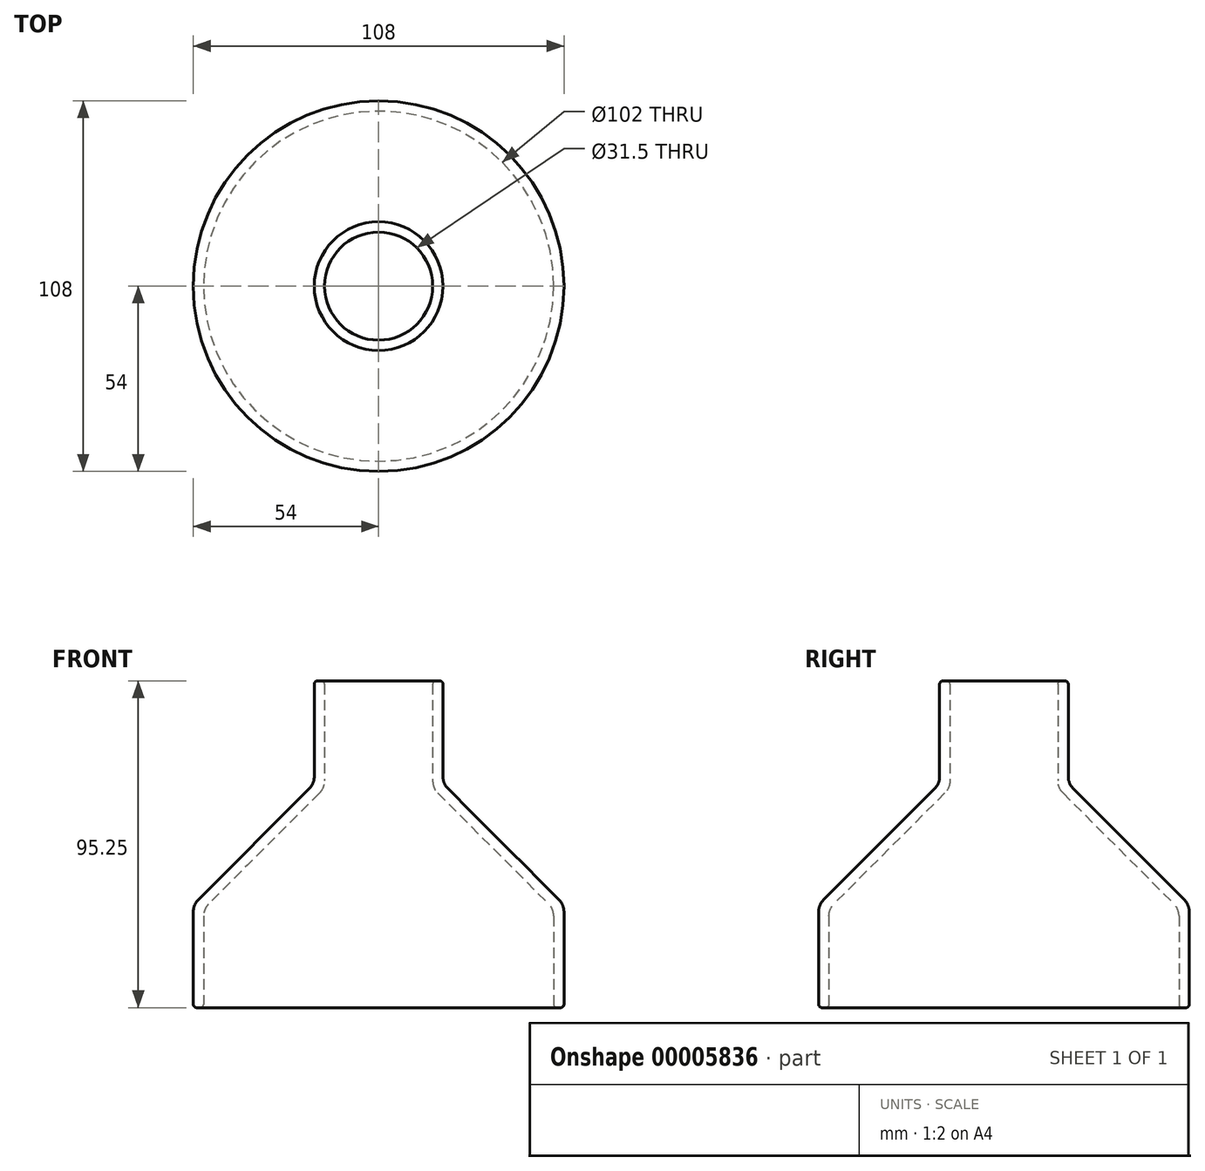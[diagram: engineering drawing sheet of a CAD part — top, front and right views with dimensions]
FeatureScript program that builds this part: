
annotation { "Feature Type Name" : "Feature", "Feature Type Description" : "" }
export const myFeature = defineFeature(function(context is Context, id is Id, definition is map)
    precondition{}
    {
        {
            var Q0;
            Q0=qCreatedBy(makeId("Front.planeOp"),FACE);
            var sketch = newSketch(context, id + "F0", { "sketchPlane" : qUnion([Q0])});
            skLineSegment(sketch, "E0", {"start": v(0, 0) * mm, "end": v(0, 22.88) * mm, "construction": true});
            skLineSegment(sketch, "E1", {"start": v(-51, 0) * mm, "end": v(0, 0) * mm, "construction": true});
            skLineSegment(sketch, "E2", {"start": v(0, 0) * mm, "end": v(51, 0) * mm, "construction": true});
            skLineSegment(sketch, "E3.bottom", {"start": v(-51, 0) * mm, "end": v(-54, 0) * mm});
            skLineSegment(sketch, "E3.left", {"start": v(-51, 0) * mm, "end": v(-51, 28.76) * mm});
            skLineSegment(sketch, "E3.right", {"start": v(-54, 0) * mm, "end": v(-54, 30) * mm});
            skLineSegment(sketch, "E4.bottom", {"start": v(-18.75, 95.25) * mm, "end": v(-15.75, 95.25) * mm});
            skLineSegment(sketch, "E4.left", {"start": v(-18.75, 95.25) * mm, "end": v(-18.75, 65.25) * mm});
            skLineSegment(sketch, "E4.right", {"start": v(-15.75, 95.25) * mm, "end": v(-15.75, 64) * mm});
            skLineSegment(sketch, "E5.MirrorCS", {"start": v(18.75, 95.25) * mm, "end": v(15.75, 95.25) * mm});
            skLineSegment(sketch, "E6.MirrorCS", {"start": v(51, 28.76) * mm, "end": v(54, 30) * mm});
            skLineSegment(sketch, "E7.MirrorCS", {"start": v(51, 0) * mm, "end": v(54, 0) * mm});
            skLineSegment(sketch, "E8.MirrorCS", {"start": v(18.75, 65.25) * mm, "end": v(15.75, 64) * mm});
            skLineSegment(sketch, "E9.MirrorCS", {"start": v(54, 0) * mm, "end": v(54, 30) * mm});
            skLineSegment(sketch, "E10.MirrorCS", {"start": v(51, 0) * mm, "end": v(51, 28.76) * mm});
            skLineSegment(sketch, "E11.MirrorCS", {"start": v(15.75, 95.25) * mm, "end": v(15.75, 64) * mm});
            skLineSegment(sketch, "E12.MirrorCS", {"start": v(18.75, 95.25) * mm, "end": v(18.75, 65.25) * mm});
            skLineSegment(sketch, "E13", {"start": v(-51, 28.76) * mm, "end": v(-15.75, 64) * mm});
            skLineSegment(sketch, "E14", {"start": v(-54, 30) * mm, "end": v(-18.75, 65.25) * mm});
            skLineSegment(sketch, "E15.MirrorCS", {"start": v(54, 30) * mm, "end": v(18.75, 65.25) * mm});
            skLineSegment(sketch, "E16.MirrorCS", {"start": v(51, 28.76) * mm, "end": v(15.75, 64) * mm});
            skSolve(sketch);
        }
        {
            var Q0;
            Q0=makeQuery(id+"F0.imprint","IMPRINT",FACE,{"disambiguationData":[TD([[makeQuery(id+"F0.imprint","IMPRINT",EDGE,{"derivedFrom":sQuery(id+"F0.wireOp",EDGE,"E3.bottom")}),-1.0]])]});
            var Q1;
            Q1=sQuery(id+"F0.wireOp",EDGE,"E0");
            revolve(context, id + "F1", {"surfaceOperationType" : NewSurfaceOperationType.NEW, "entities" : qUnion([Q0]), "axis" : qUnion([Q1]), "revolveType" : RevolveType.FULL});
        }
        {
            var Q0;
            Q0=makeQuery(id+"F1.opRevolve","SWEPT_EDGE",EDGE,{"disambiguationData":[OSD([sQuery(id+"F0.wireOp",EDGE,"E4.left"),sQuery(id+"F0.wireOp",EDGE,"E14")])]});
            var Q1;
            Q1=makeQuery(id+"F1.opRevolve","SWEPT_EDGE",EDGE,{"disambiguationData":[OSD([sQuery(id+"F0.wireOp",EDGE,"E3.right"),sQuery(id+"F0.wireOp",EDGE,"E14")])]});
            var Q2;
            Q2=makeQuery(id+"F1.opRevolve","SWEPT_EDGE",EDGE,{"disambiguationData":[OSD([sQuery(id+"F0.wireOp",EDGE,"E3.left"),sQuery(id+"F0.wireOp",EDGE,"E13")])]});
            var Q3;
            Q3=makeQuery(id+"F1.opRevolve","SWEPT_EDGE",EDGE,{"disambiguationData":[OSD([sQuery(id+"F0.wireOp",EDGE,"E4.right"),sQuery(id+"F0.wireOp",EDGE,"E13")])]});
            fillet(context, id + "F2", {"entities" : qUnion([Q0, Q1, Q2, Q3]), "radius" : 5 * mm, "tangentPropagation" : true, "allowEdgeOverflow" : false});
        }
        {
            var Q0;
            Q0=makeQuery(id+"F1.opRevolve","SWEPT_FACE",FACE,{"disambiguationData":[OSD([sQuery(id+"F0.wireOp",EDGE,"E3.bottom")])]});
            var Q1;
            Q1=makeQuery(id+"F1.opRevolve","SWEPT_FACE",FACE,{"disambiguationData":[OSD([sQuery(id+"F0.wireOp",EDGE,"E4.bottom")])]});
            fillet(context, id + "F3", {"entities" : qUnion([Q0, Q1]), "radius" : 1 * mm, "tangentPropagation" : true, "allowEdgeOverflow" : false});
        }
    });
